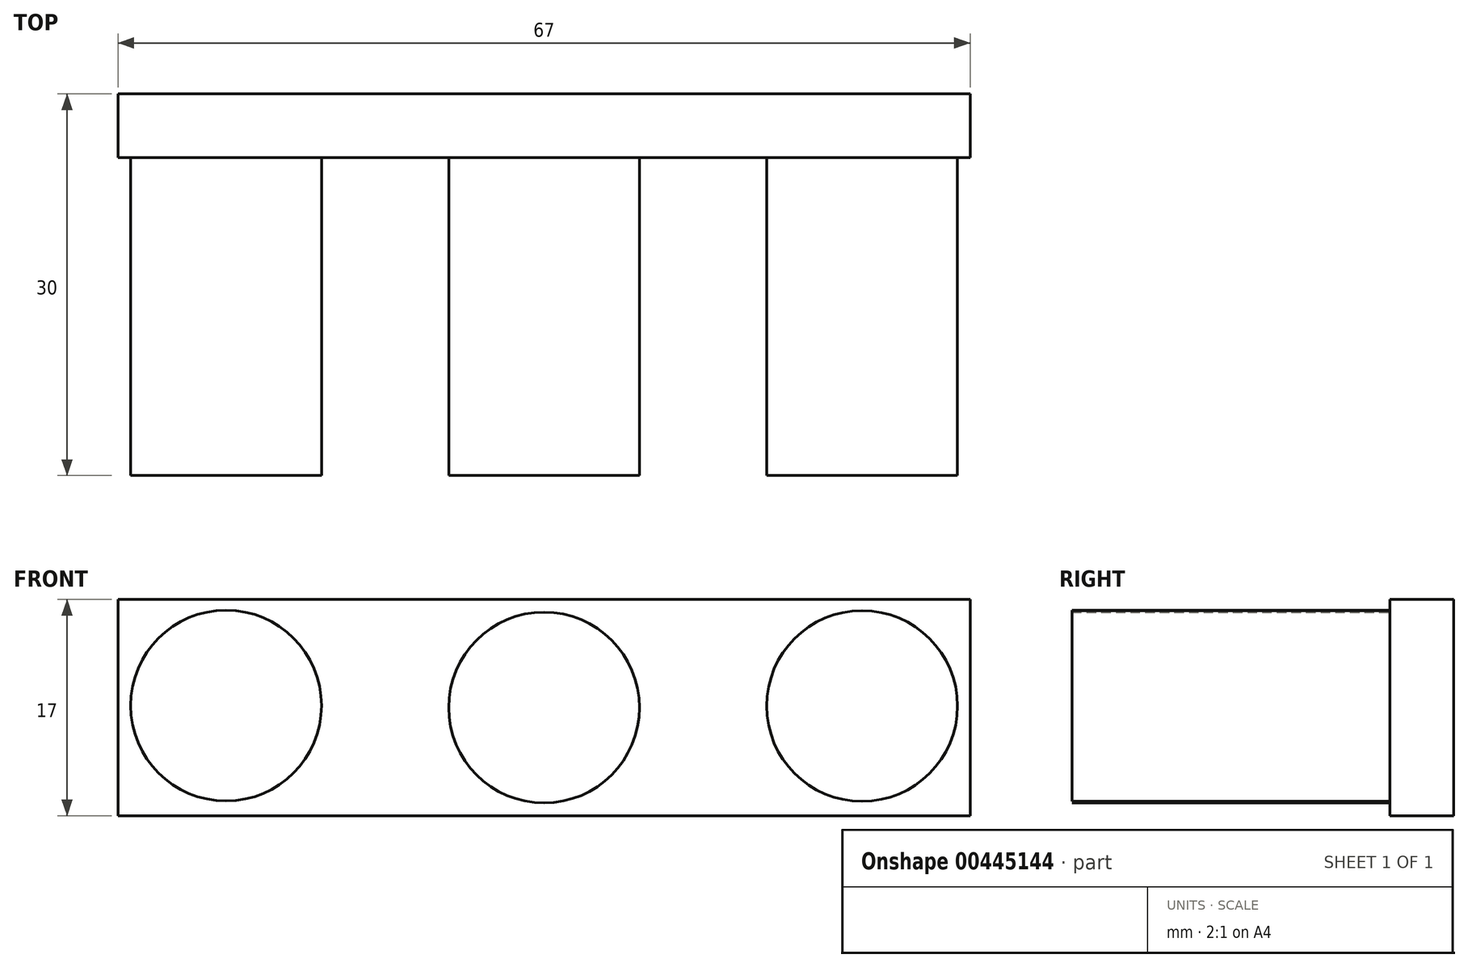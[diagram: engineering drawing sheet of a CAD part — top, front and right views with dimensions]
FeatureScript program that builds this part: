
annotation { "Feature Type Name" : "Feature", "Feature Type Description" : "" }
export const myFeature = defineFeature(function(context is Context, id is Id, definition is map)
    precondition{}
    {
        {
            var Q0;
            Q0=qCreatedBy(makeId("Front.planeOp"),FACE);
            var sketch = newSketch(context, id + "F0", { "sketchPlane" : qUnion([Q0])});
            skLineSegment(sketch, "E0.bottom", {"start": v(33.5, 8.5) * mm, "end": v(-33.5, 8.5) * mm});
            skLineSegment(sketch, "E0.top", {"start": v(33.5, -8.5) * mm, "end": v(-33.5, -8.5) * mm});
            skLineSegment(sketch, "E0.left", {"start": v(33.5, 8.5) * mm, "end": v(33.5, -8.5) * mm});
            skLineSegment(sketch, "E0.right", {"start": v(-33.5, 8.5) * mm, "end": v(-33.5, -8.5) * mm});
            skPoint(sketch, "E0.middle", {"position": v(0, 0) * mm});
            skCircle(sketch, "E1", {"center": v(0, 0) * mm, "radius": 7.5 * mm});
            skLineSegment(sketch, "E2", {"start": v(-7.5, 0) * mm, "end": v(-17.5, 0) * mm});
            skLineSegment(sketch, "E3", {"start": v(7.5, 0) * mm, "end": v(17.5, 0) * mm});
            skCircle(sketch, "E4", {"center": v(25, 0.12) * mm, "radius": 7.5 * mm});
            skPoint(sketch, "E4.first.point", {"position": v(32.5, 0) * mm});
            skPoint(sketch, "E4.third.point", {"position": v(25.3, -7.37) * mm});
            skCircle(sketch, "E5", {"center": v(-25, 0.15) * mm, "radius": 7.5 * mm});
            skPoint(sketch, "E5.second.point", {"position": v(-32.5, 0) * mm});
            skPoint(sketch, "E5.third.point", {"position": v(-26.33, -7.23) * mm});
            skSolve(sketch);
        }
        {
            var Q0;
            Q0=makeQuery(id+"F0.imprint","IMPRINT",FACE,{"disambiguationData":[TD([[makeQuery(id+"F0.imprint","IMPRINT",EDGE,{"derivedFrom":sQuery(id+"F0.wireOp",EDGE,"E0.bottom")}),1.0]])]});
            extrude(context, id + "F1", {"entities" : qUnion([Q0]), "depth" : 5 * mm});
        }
        {
            var Q0;
            Q0=makeQuery(id+"F0.imprint","IMPRINT",FACE,{"disambiguationData":[TD([[makeQuery(id+"F0.imprint","IMPRINT",EDGE,{"derivedFrom":sQuery(id+"F0.wireOp",EDGE,"E5")}),1.0]])]});
            extrude(context, id + "F2", {"entities" : qUnion([Q0]), "operationType" : NewBodyOperationType.ADD, "depth" : 30 * mm});
        }
        {
            var Q0;
            {var subQ0=sQuery(id+"F0.wireOp",EDGE,"E1");var subQ1=makeQuery(id+"F0.imprint","IMPRINT",VERTEX,{"disambiguationData":[OD(0.0)],"derivedFrom":subQ0});Q0=makeQuery(id+"F0.imprint","IMPRINT",FACE,{"disambiguationData":[TD([[makeQuery(id+"F0.imprint","IMPRINT",EDGE,{"disambiguationData":[TD([[subQ1,1.0]])],"derivedFrom":subQ0}),1.0]])]});}
            var Q1;
            Q1=makeQuery(id+"F0.imprint","IMPRINT",FACE,{"disambiguationData":[TD([[makeQuery(id+"F0.imprint","IMPRINT",EDGE,{"derivedFrom":sQuery(id+"F0.wireOp",EDGE,"E4")}),1.0]])]});
            extrude(context, id + "F3", {"entities" : qUnion([Q0, Q1]), "operationType" : NewBodyOperationType.ADD, "depth" : 30 * mm});
        }
    });
